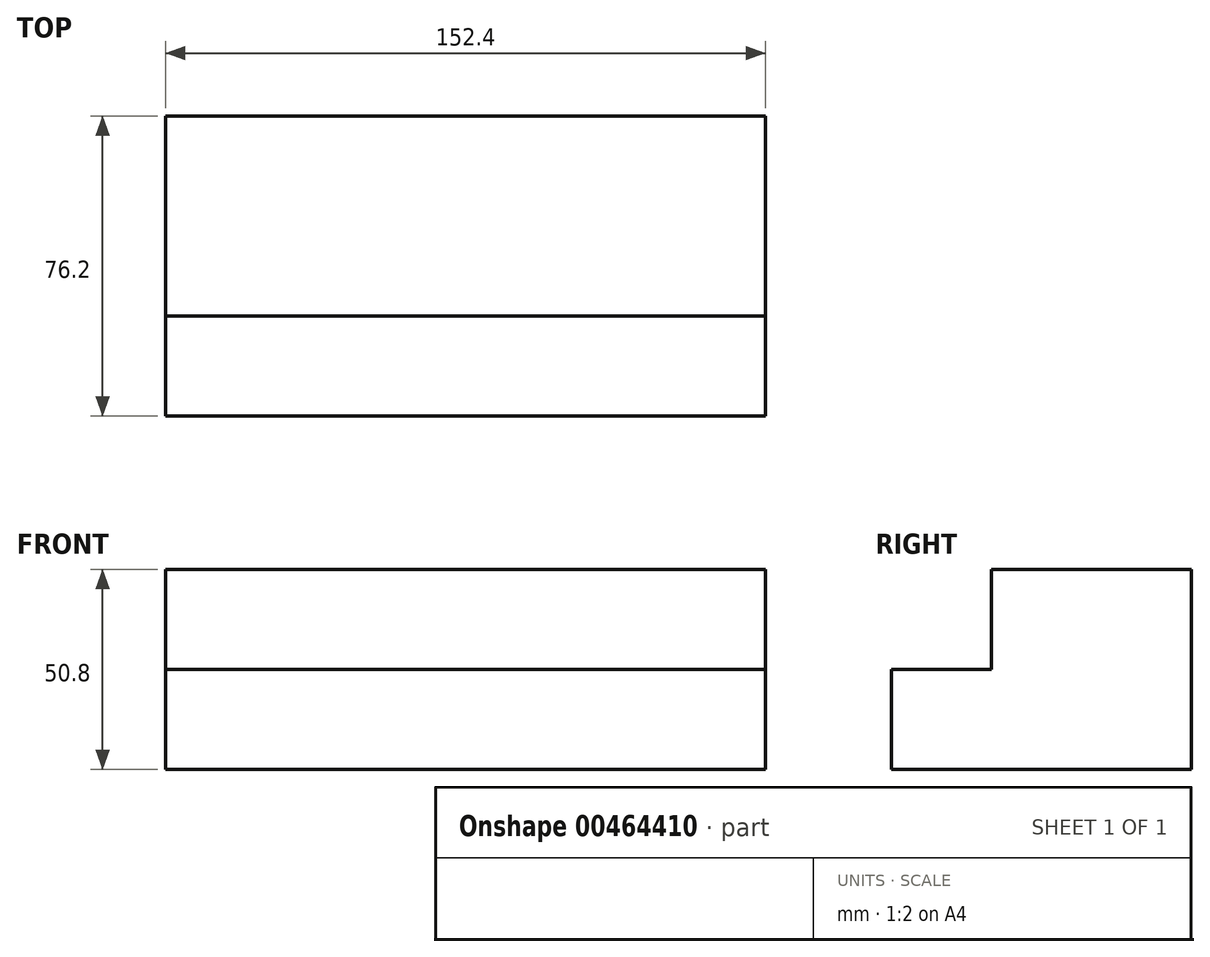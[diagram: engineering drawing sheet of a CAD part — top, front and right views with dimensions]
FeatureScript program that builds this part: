
annotation { "Feature Type Name" : "Feature", "Feature Type Description" : "" }
export const myFeature = defineFeature(function(context is Context, id is Id, definition is map)
    precondition{}
    {
        {
            var Q0;
            Q0=qCreatedBy(makeId("Right.planeOp"),FACE);
            var sketch = newSketch(context, id + "F0", { "sketchPlane" : qUnion([Q0])});
            skLineSegment(sketch, "E0", {"start": v(101.6, 50.76) * mm, "end": v(50.8, 50.76) * mm});
            skLineSegment(sketch, "E1", {"start": v(50.8, 50.76) * mm, "end": v(50.8, 25.36) * mm});
            skLineSegment(sketch, "E2", {"start": v(50.8, 25.36) * mm, "end": v(25.4, 25.36) * mm});
            skLineSegment(sketch, "E3", {"start": v(25.4, 25.36) * mm, "end": v(25.4, -0.04) * mm});
            skLineSegment(sketch, "E4", {"start": v(25.4, -0.04) * mm, "end": v(101.6, -0.04) * mm});
            skLineSegment(sketch, "E5", {"start": v(101.6, -0.04) * mm, "end": v(101.6, 50.76) * mm});
            skSolve(sketch);
        }
        {
            var Q0;
            Q0=makeQuery(id+"F0.imprint","IMPRINT",FACE,{"disambiguationData":[TD([[makeQuery(id+"F0.imprint","IMPRINT",EDGE,{"derivedFrom":sQuery(id+"F0.wireOp",EDGE,"E0")}),1.0]])]});
            extrude(context, id + "F1", {"entities" : qUnion([Q0]), "depth" : 152.4 * mm});
        }
    });
